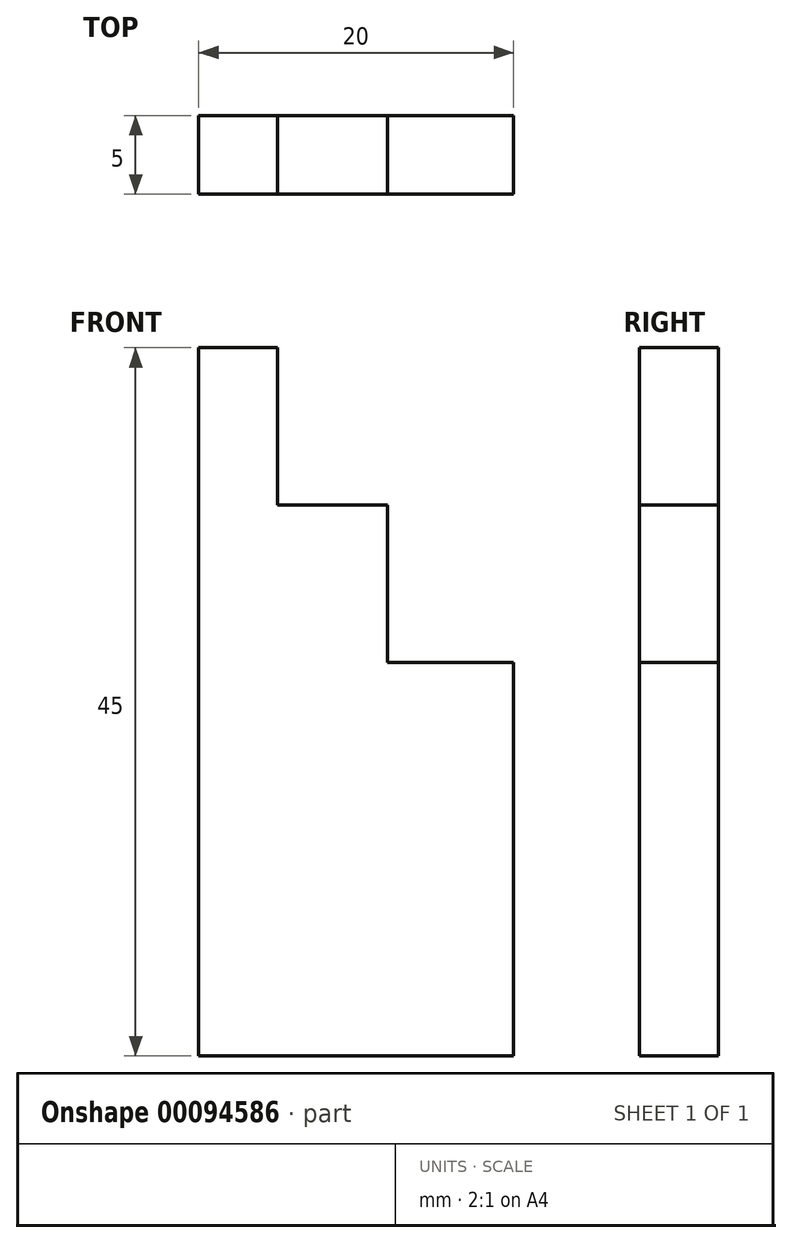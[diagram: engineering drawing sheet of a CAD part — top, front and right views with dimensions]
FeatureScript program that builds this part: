
annotation { "Feature Type Name" : "Feature", "Feature Type Description" : "" }
export const myFeature = defineFeature(function(context is Context, id is Id, definition is map)
    precondition{}
    {
        {
            var Q0;
            Q0=qCreatedBy(makeId("Front.planeOp"),FACE);
            var sketch = newSketch(context, id + "F0", { "sketchPlane" : qUnion([Q0])});
            skLineSegment(sketch, "E0", {"start": v(-12, -25) * mm, "end": v(8, -25) * mm});
            skLineSegment(sketch, "E1", {"start": v(8, -25) * mm, "end": v(8, 0) * mm});
            skLineSegment(sketch, "E2", {"start": v(-12, -25) * mm, "end": v(-12, 20) * mm});
            skLineSegment(sketch, "E3", {"start": v(-12, 20) * mm, "end": v(-7, 20) * mm});
            skLineSegment(sketch, "E4", {"start": v(-7, 20) * mm, "end": v(-7, 10) * mm});
            skLineSegment(sketch, "E5", {"start": v(-7, 10) * mm, "end": v(0, 10) * mm});
            skLineSegment(sketch, "E6", {"start": v(0, 10) * mm, "end": v(0, 0) * mm});
            skLineSegment(sketch, "E7", {"start": v(0, 0) * mm, "end": v(8, 0) * mm});
            skSolve(sketch);
        }
        {
            var Q0;
            Q0 = qSketchRegion(id + "F0", true);
            extrude(context, id + "F1", {"entities" : qUnion([Q0]), "depth" : 5 * mm});
        }
    });
